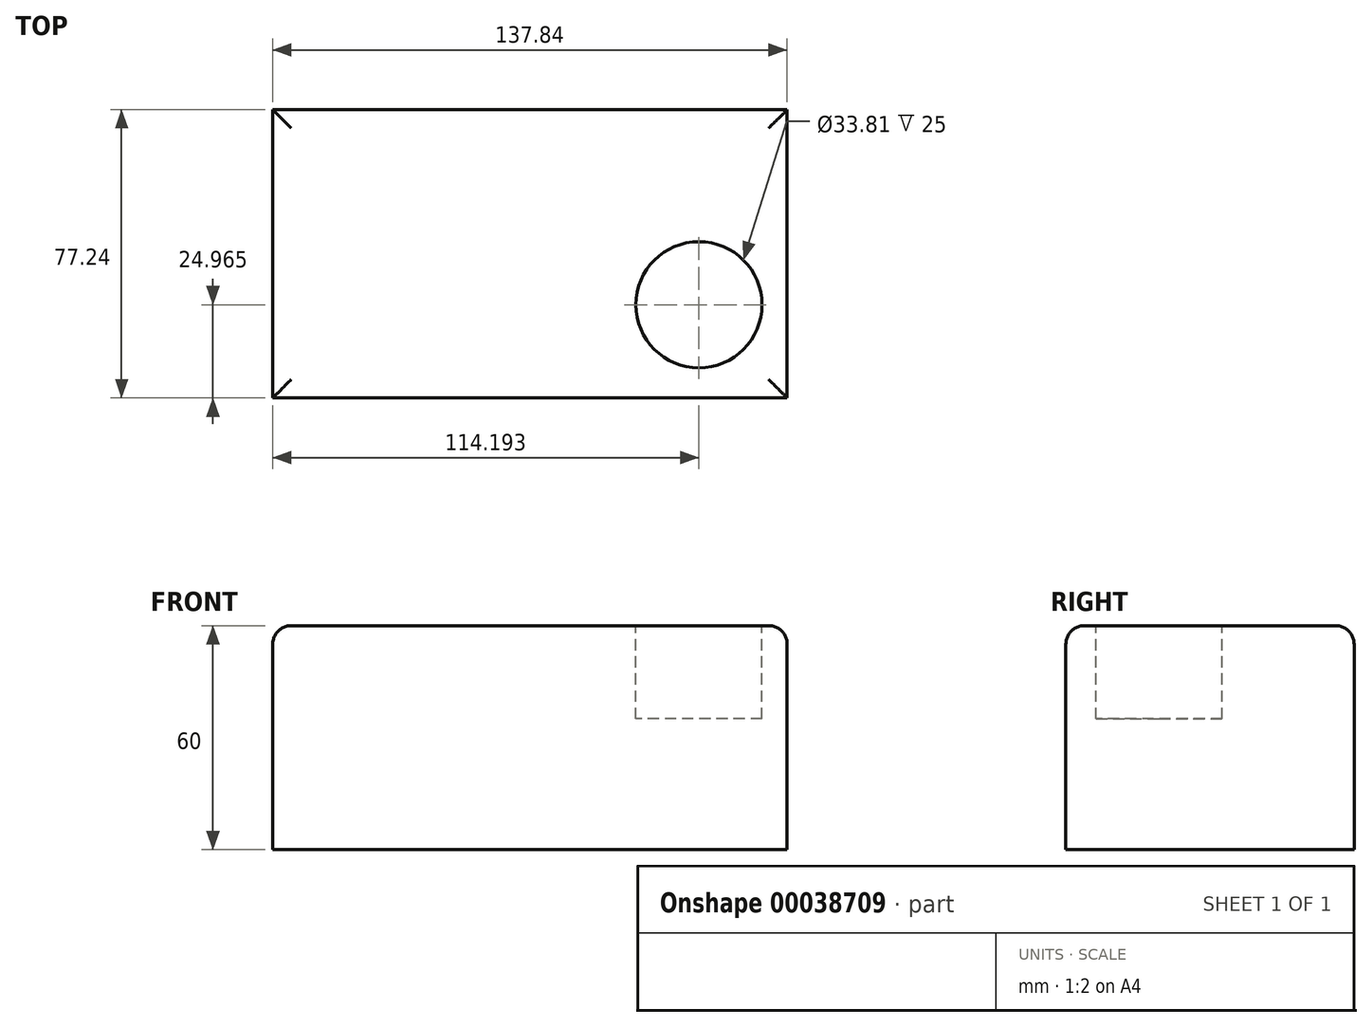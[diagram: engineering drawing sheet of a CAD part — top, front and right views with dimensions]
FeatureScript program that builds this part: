
annotation { "Feature Type Name" : "Feature", "Feature Type Description" : "" }
export const myFeature = defineFeature(function(context is Context, id is Id, definition is map)
    precondition{}
    {
        {
            var Q0;
            Q0=qCreatedBy(makeId("Top.planeOp"),FACE);
            var sketch = newSketch(context, id + "F0", { "sketchPlane" : qUnion([Q0])});
            skLineSegment(sketch, "E0.bottom", {"start": v(-68.25, -29.92) * mm, "end": v(69.6, -29.92) * mm});
            skLineSegment(sketch, "E0.top", {"start": v(-68.25, 47.32) * mm, "end": v(69.6, 47.32) * mm});
            skLineSegment(sketch, "E0.left", {"start": v(-68.25, -29.92) * mm, "end": v(-68.25, 47.32) * mm});
            skLineSegment(sketch, "E0.right", {"start": v(69.6, -29.92) * mm, "end": v(69.6, 47.32) * mm});
            skSolve(sketch);
        }
        {
            var Q0;
            Q0=makeQuery(id+"F0.imprint","IMPRINT",FACE,{"disambiguationData":[TD([[makeQuery(id+"F0.imprint","IMPRINT",EDGE,{"derivedFrom":sQuery(id+"F0.wireOp",EDGE,"E0.bottom")}),1.0]])]});
            extrude(context, id + "F1", {"entities" : qUnion([Q0]), "depth" : 60 * mm});
        }
        {
            var Q0;
            Q0=makeQuery(id+"F1.opExtrude","CAP_FACE",FACE,{"disambiguationData":[OSD([sQuery(id+"F0.wireOp",EDGE,"E0.bottom"),sQuery(id+"F0.wireOp",EDGE,"E0.top"),sQuery(id+"F0.wireOp",EDGE,"E0.left"),sQuery(id+"F0.wireOp",EDGE,"E0.right")])],"isStart":false});
            var sketch = newSketch(context, id + "F2", { "sketchPlane" : qUnion([Q0])});
            skCircle(sketch, "E1", {"center": v(45.94, -4.95) * mm, "radius": 16.9 * mm});
            skSolve(sketch);
        }
        {
            var Q0;
            Q0=makeQuery(id+"F2.imprint","IMPRINT",FACE,{"disambiguationData":[TD([[makeQuery(id+"F2.imprint","IMPRINT",EDGE,{"derivedFrom":sQuery(id+"F2.wireOp",EDGE,"E1")}),1.0]])]});
            extrude(context, id + "F3", {"entities" : qUnion([Q0]), "operationType" : NewBodyOperationType.REMOVE, "oppositeDirection" : true, "depth" : 25 * mm});
        }
        {
            var Q0;
            Q0=makeQuery(id+"F1.opExtrude","CAP_EDGE",EDGE,{"disambiguationData":[OSD([sQuery(id+"F0.wireOp",EDGE,"E0.bottom")])],"isStart":false});
            var Q1;
            Q1=makeQuery(id+"F1.opExtrude","CAP_EDGE",EDGE,{"disambiguationData":[OSD([sQuery(id+"F0.wireOp",EDGE,"E0.right")])],"isStart":false});
            var Q2;
            Q2=makeQuery(id+"F1.opExtrude","CAP_EDGE",EDGE,{"disambiguationData":[OSD([sQuery(id+"F0.wireOp",EDGE,"E0.top")])],"isStart":false});
            var Q3;
            Q3=makeQuery(id+"F1.opExtrude","CAP_EDGE",EDGE,{"disambiguationData":[OSD([sQuery(id+"F0.wireOp",EDGE,"E0.left")])],"isStart":false});
            fillet(context, id + "F4", {"entities" : qUnion([Q0, Q1, Q2, Q3]), "radius" : 5 * mm, "tangentPropagation" : true, "allowEdgeOverflow" : false});
        }
    });
